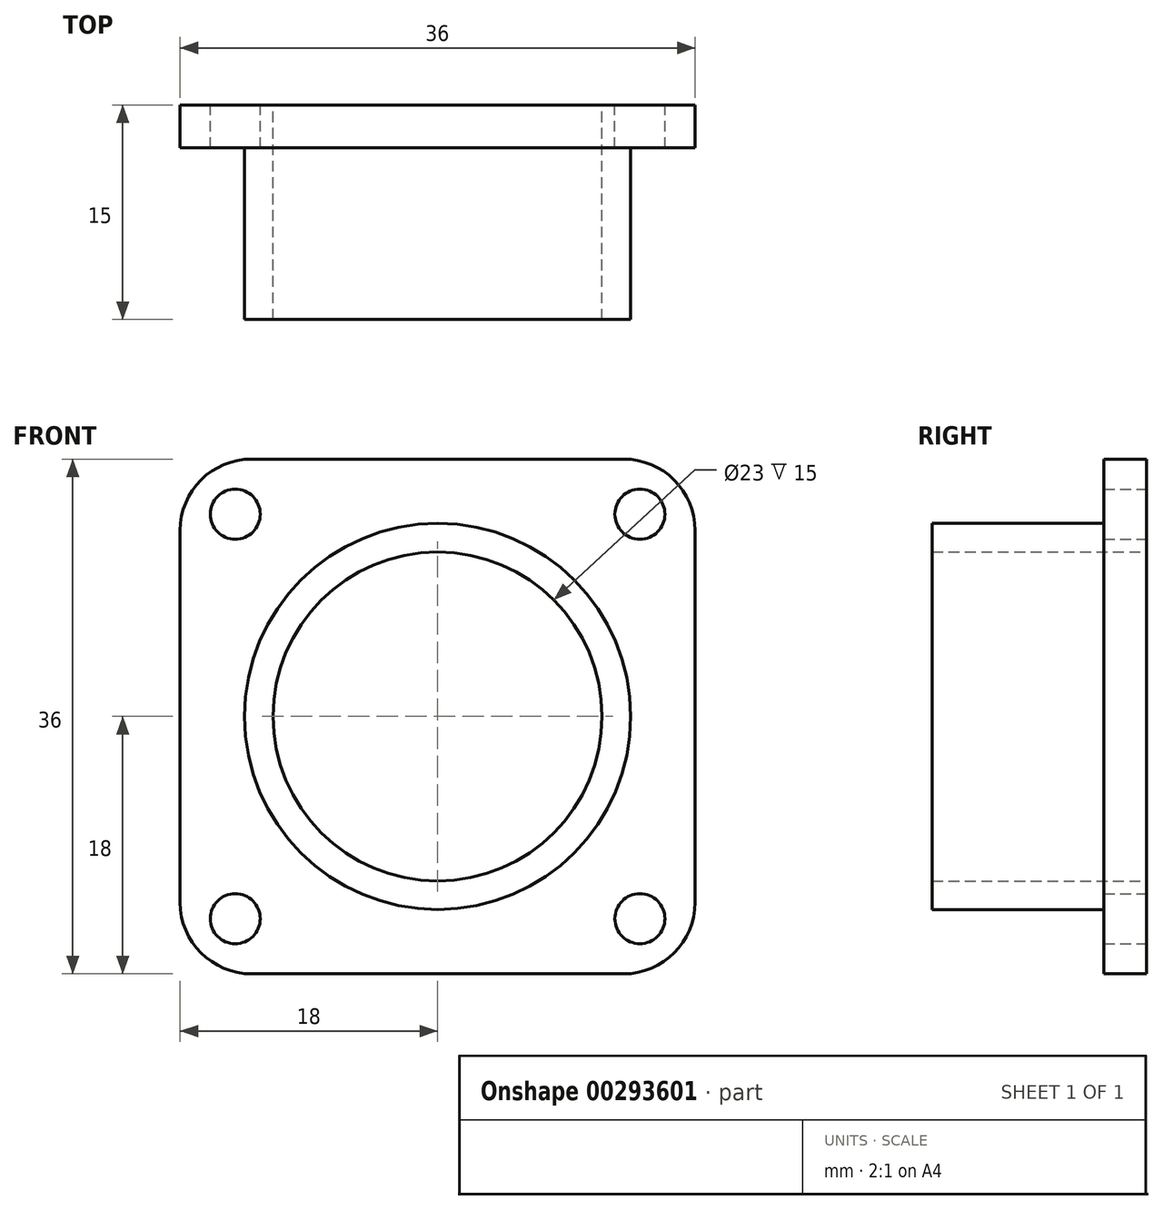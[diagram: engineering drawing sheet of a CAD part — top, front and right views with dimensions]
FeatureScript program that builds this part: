
annotation { "Feature Type Name" : "Feature", "Feature Type Description" : "" }
export const myFeature = defineFeature(function(context is Context, id is Id, definition is map)
    precondition{}
    {
        {
            var Q0;
            Q0=qCreatedBy(makeId("Front.planeOp"),FACE);
            var sketch = newSketch(context, id + "F0", { "sketchPlane" : qUnion([Q0])});
            skCircle(sketch, "E0", {"center": v(0, 0) * mm, "radius": 11.5 * mm});
            skCircle(sketch, "E1", {"center": v(0, 0) * mm, "radius": 13.5 * mm});
            skLineSegment(sketch, "E2.bottom", {"start": v(-18, 18) * mm, "end": v(18, 18) * mm});
            skLineSegment(sketch, "E2.top", {"start": v(-18, -18) * mm, "end": v(18, -18) * mm});
            skLineSegment(sketch, "E2.left", {"start": v(-18, 18) * mm, "end": v(-18, -18) * mm});
            skLineSegment(sketch, "E2.right", {"start": v(18, 18) * mm, "end": v(18, -18) * mm});
            skLineSegment(sketch, "E3", {"start": v(0, 0) * mm, "end": v(-18, 18) * mm, "construction": true});
            skLineSegment(sketch, "E4", {"start": v(0, 0) * mm, "end": v(18, 18) * mm, "construction": true});
            skLineSegment(sketch, "E5", {"start": v(0, 0) * mm, "end": v(18, -18) * mm, "construction": true});
            skLineSegment(sketch, "E6", {"start": v(0, 0) * mm, "end": v(-18, -18) * mm, "construction": true});
            skCircle(sketch, "E7", {"center": v(0, 0) * mm, "radius": 20 * mm, "construction": true});
            skCircle(sketch, "E8", {"center": v(-14.14, 14.14) * mm, "radius": 1.75 * mm});
            skLineSegment(sketch, "E9", {"start": v(0, 0) * mm, "end": v(0, 36.59) * mm, "construction": true});
            skCircle(sketch, "E10.1.0", {"center": v(-14.14, -14.14) * mm, "radius": 1.75 * mm});
            skCircle(sketch, "E10.2.0", {"center": v(14.14, -14.14) * mm, "radius": 1.75 * mm});
            skCircle(sketch, "E10.3.0", {"center": v(14.14, 14.14) * mm, "radius": 1.75 * mm});
            skSolve(sketch);
        }
        {
            var Q0;
            Q0=makeQuery(id+"F0.imprint","IMPRINT",FACE,{"disambiguationData":[TD([[makeQuery(id+"F0.imprint","IMPRINT",EDGE,{"derivedFrom":sQuery(id+"F0.wireOp",EDGE,"E0")}),-1.0]])]});
            extrude(context, id + "F1", {"entities" : qUnion([Q0]), "depth" : 15 * mm});
        }
        {
            var Q0;
            Q0=makeQuery(id+"F0.imprint","IMPRINT",FACE,{"disambiguationData":[TD([[makeQuery(id+"F0.imprint","IMPRINT",EDGE,{"derivedFrom":sQuery(id+"F0.wireOp",EDGE,"E1")}),-1.0]])]});
            extrude(context, id + "F2", {"entities" : qUnion([Q0]), "operationType" : NewBodyOperationType.ADD, "depth" : 3 * mm});
        }
        {
            var Q0;
            Q0=makeQuery(id+"F2.opExtrude","SWEPT_EDGE",EDGE,{"disambiguationData":[OSD([sQuery(id+"F0.wireOp",EDGE,"E2.top"),sQuery(id+"F0.wireOp",EDGE,"E2.right")])]});
            var Q1;
            Q1=makeQuery(id+"F2.opExtrude","SWEPT_EDGE",EDGE,{"disambiguationData":[OSD([sQuery(id+"F0.wireOp",EDGE,"E2.bottom"),sQuery(id+"F0.wireOp",EDGE,"E2.right")])]});
            var Q2;
            Q2=makeQuery(id+"F2.opExtrude","SWEPT_EDGE",EDGE,{"disambiguationData":[OSD([sQuery(id+"F0.wireOp",EDGE,"E2.bottom"),sQuery(id+"F0.wireOp",EDGE,"E2.left")])]});
            var Q3;
            Q3=makeQuery(id+"F2.opExtrude","SWEPT_EDGE",EDGE,{"disambiguationData":[OSD([sQuery(id+"F0.wireOp",EDGE,"E2.top"),sQuery(id+"F0.wireOp",EDGE,"E2.left")])]});
            fillet(context, id + "F3", {"entities" : qUnion([Q0, Q1, Q2, Q3]), "radius" : 5 * mm, "tangentPropagation" : true, "allowEdgeOverflow" : false});
        }
    });
